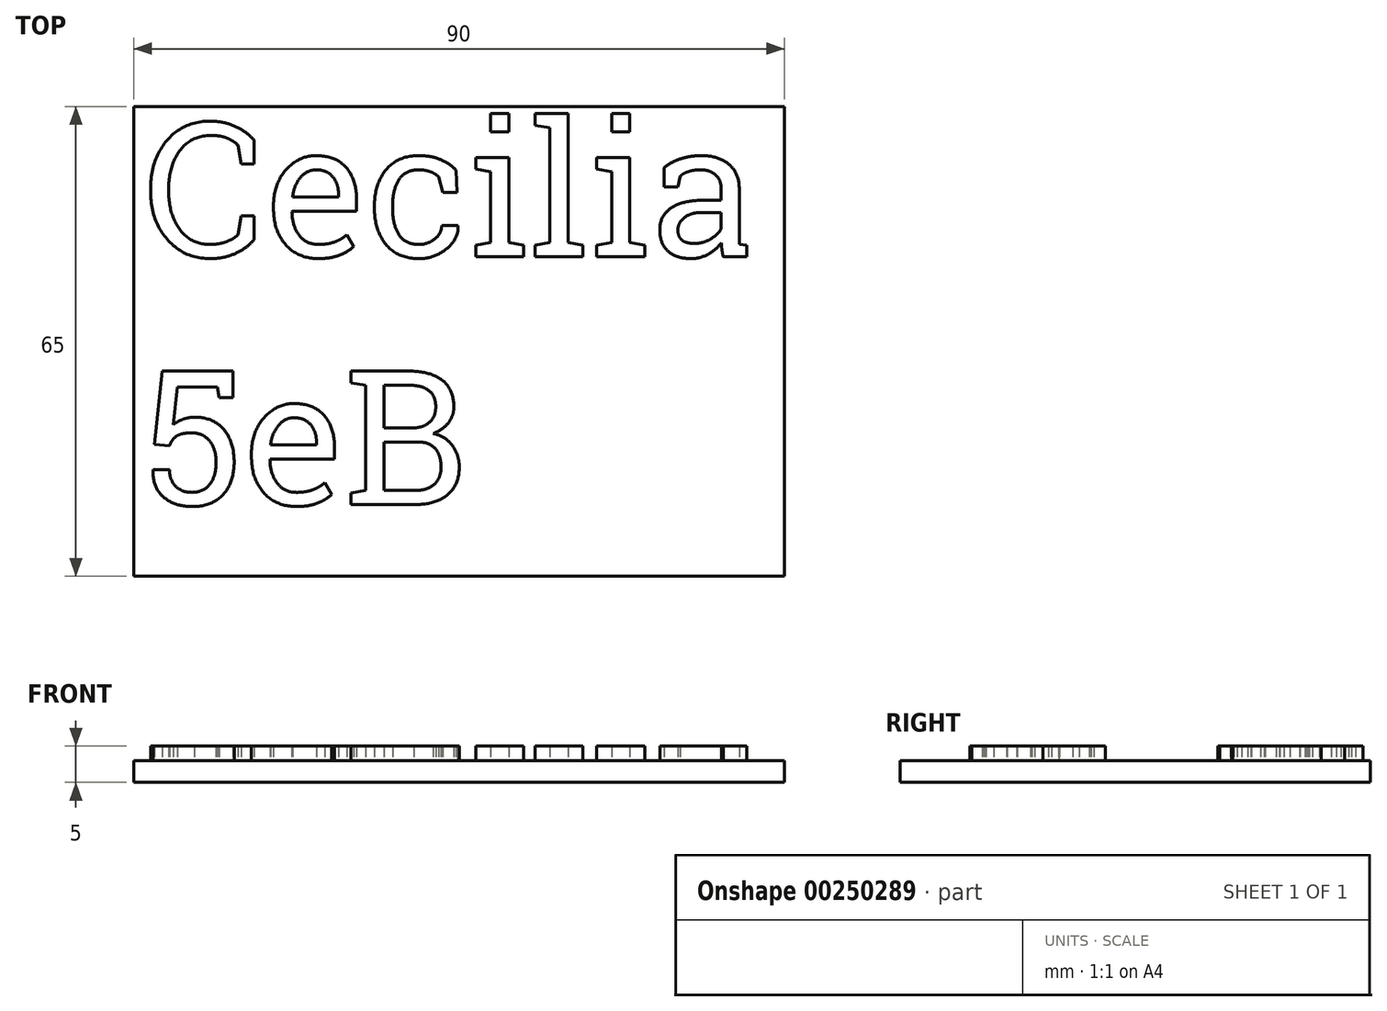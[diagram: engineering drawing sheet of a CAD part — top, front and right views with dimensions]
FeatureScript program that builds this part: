
annotation { "Feature Type Name" : "Feature", "Feature Type Description" : "" }
export const myFeature = defineFeature(function(context is Context, id is Id, definition is map)
    precondition{}
    {
        {
            var Q0;
            Q0=qCreatedBy(makeId("Top.planeOp"),FACE);
            var sketch = newSketch(context, id + "F0", { "sketchPlane" : qUnion([Q0])});
            skLineSegment(sketch, "E0.bottom", {"start": v(0, 0) * mm, "end": v(90, 0) * mm});
            skLineSegment(sketch, "E0.top", {"start": v(0, -65) * mm, "end": v(90, -65) * mm});
            skLineSegment(sketch, "E0.left", {"start": v(0, 0) * mm, "end": v(0, -65) * mm});
            skLineSegment(sketch, "E0.right", {"start": v(90, 0) * mm, "end": v(90, -65) * mm});
            skSolve(sketch);
        }
        {
            var Q0;
            Q0=makeQuery(id+"F0.imprint","IMPRINT",FACE,{"disambiguationData":[TD([[makeQuery(id+"F0.imprint","IMPRINT",EDGE,{"derivedFrom":sQuery(id+"F0.wireOp",EDGE,"E0.bottom")}),-1.0]])]});
            extrude(context, id + "F1", {"entities" : qUnion([Q0]), "depth" : 3 * mm});
        }
        {
            var Q0;
            Q0=makeQuery(id+"F1.opExtrude","CAP_FACE",FACE,{"disambiguationData":[OSD([sQuery(id+"F0.wireOp",EDGE,"E0.bottom"),sQuery(id+"F0.wireOp",EDGE,"E0.top"),sQuery(id+"F0.wireOp",EDGE,"E0.left"),sQuery(id+"F0.wireOp",EDGE,"E0.right")])],"isStart":false});
            var sketch = newSketch(context, id + "F2", { "sketchPlane" : qUnion([Q0])});
            skText(sketch, "E1", { "text": "Cecilia\n5eB", "fontName": "RobotoSlab-Regular.ttf"});
            const initialGuessF2  = {"E1": [0.00144, -0.02078, 1, 0, 0.01871]};
            skSetInitialGuess(sketch, initialGuessF2);
            skSolve(sketch);
        }
        {
            var Q0;
            Q0 = qSketchRegion(id + "F2", true);
            extrude(context, id + "F3", {"entities" : qUnion([Q0]), "operationType" : NewBodyOperationType.ADD, "depth" : 2 * mm});
        }
    });
